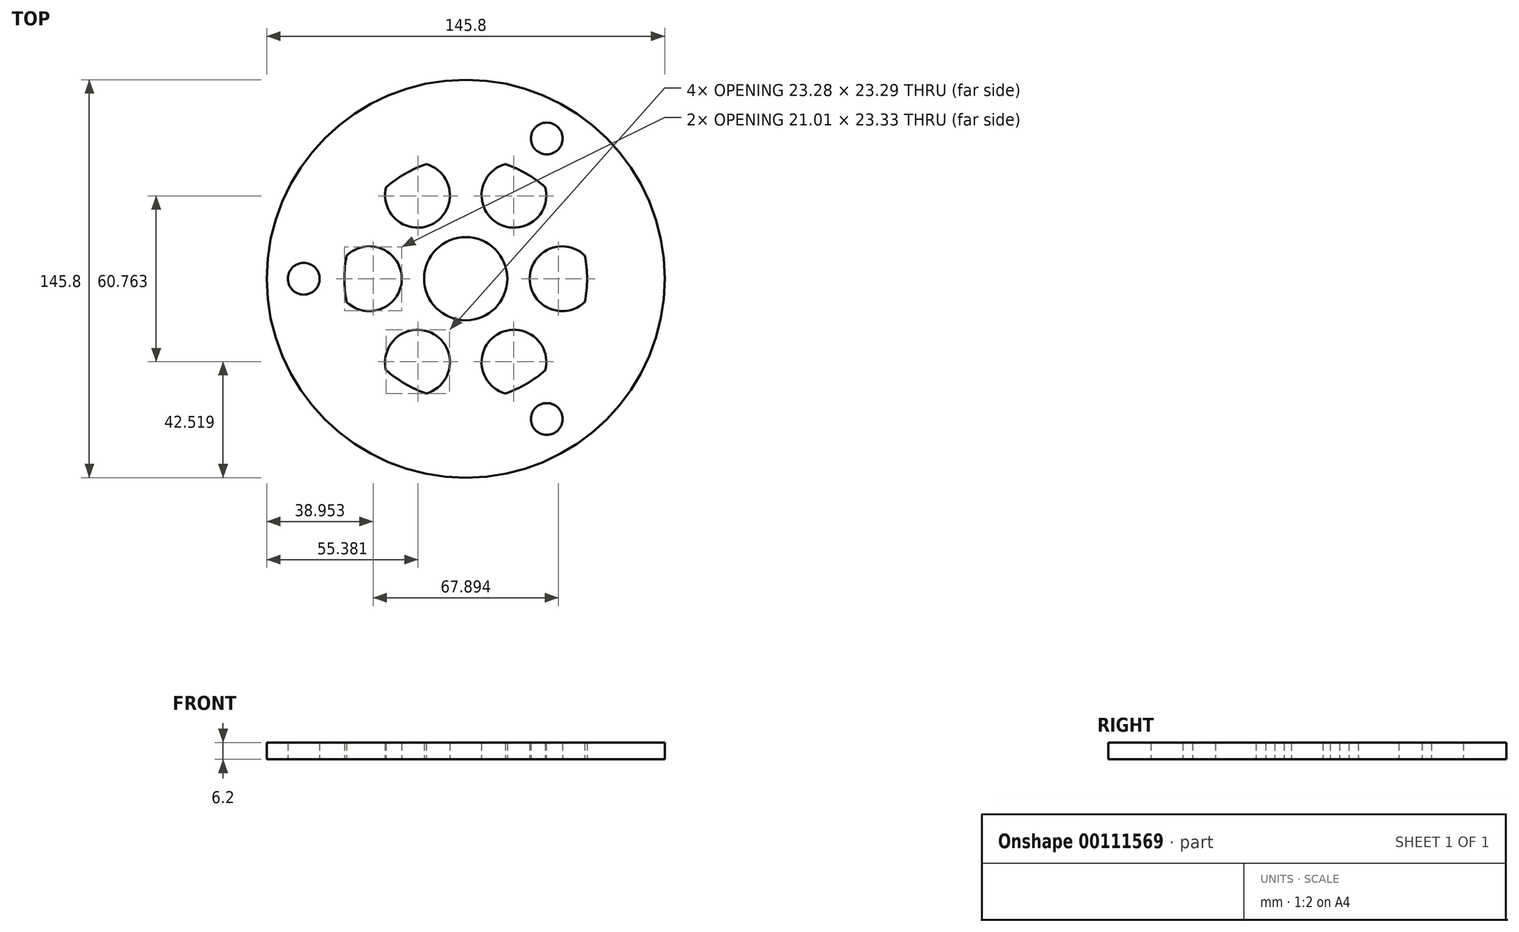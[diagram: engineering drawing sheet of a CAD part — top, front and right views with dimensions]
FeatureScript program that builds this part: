
annotation { "Feature Type Name" : "Feature", "Feature Type Description" : "" }
export const myFeature = defineFeature(function(context is Context, id is Id, definition is map)
    precondition{}
    {
        {
            var Q0;
            Q0=qCreatedBy(makeId("Top.planeOp"),FACE);
            var sketch = newSketch(context, id + "F0", { "sketchPlane" : qUnion([Q0])});
            skCircle(sketch, "E0", {"center": v(0, 0) * mm, "radius": 72.9 * mm});
            skCircle(sketch, "E1", {"center": v(0, 0) * mm, "radius": 15.24 * mm});
            skArc(sketch, "E2", {"start": v(-14.48, 42.03) * mm, "mid": v(-22.23, 38.5) * mm, "end": v(-29.16, 33.55) * mm});
            skArc(sketch, "E3", {"start": v(43.63, 8.48) * mm, "mid": v(23.44, 0) * mm, "end": v(43.63, -8.48) * mm});
            skArc(sketch, "E4.1.0", {"start": v(14.48, 42.03) * mm, "mid": v(11.72, 20.3) * mm, "end": v(29.16, 33.55) * mm});
            skArc(sketch, "E4.2.0", {"start": v(-29.16, 33.55) * mm, "mid": v(-11.72, 20.3) * mm, "end": v(-14.48, 42.03) * mm});
            skArc(sketch, "E4.3.0", {"start": v(-43.63, -8.48) * mm, "mid": v(-23.44, 0) * mm, "end": v(-43.63, 8.48) * mm});
            skArc(sketch, "E4.4.0", {"start": v(-14.48, -42.03) * mm, "mid": v(-11.72, -20.3) * mm, "end": v(-29.16, -33.55) * mm});
            skArc(sketch, "E4.5.0", {"start": v(29.16, -33.55) * mm, "mid": v(11.72, -20.3) * mm, "end": v(14.48, -42.03) * mm});
            skArc(sketch, "E5.trimOffspring", {"start": v(29.16, 33.55) * mm, "mid": v(22.23, 38.5) * mm, "end": v(14.48, 42.03) * mm});
            skArc(sketch, "E6.trimOffspring", {"start": v(43.63, -8.48) * mm, "mid": v(44.45, 0) * mm, "end": v(43.63, 8.48) * mm});
            skArc(sketch, "E7.trimOffspring", {"start": v(14.48, -42.03) * mm, "mid": v(22.22, -38.5) * mm, "end": v(29.16, -33.55) * mm});
            skArc(sketch, "E8.trimOffspring", {"start": v(-29.16, -33.55) * mm, "mid": v(-22.23, -38.5) * mm, "end": v(-14.48, -42.03) * mm});
            skArc(sketch, "E9.trimOffspring", {"start": v(-43.63, 8.48) * mm, "mid": v(-44.45, 0) * mm, "end": v(-43.63, -8.48) * mm});
            skCircle(sketch, "E10", {"center": v(-59.33, 0) * mm, "radius": 5.82 * mm});
            skPoint(sketch, "E10.centerSnap0", {"position": v(-44.45, 0) * mm});
            skCircle(sketch, "E11.1.0", {"center": v(29.67, -51.39) * mm, "radius": 5.82 * mm});
            skCircle(sketch, "E11.2.0", {"center": v(29.67, 51.39) * mm, "radius": 5.82 * mm});
            skSolve(sketch);
        }
        {
            var Q0;
            Q0 = qSketchRegion(id + "F0", true);
            extrude(context, id + "F1", {"entities" : qUnion([Q0]), "depth" : 6.2 * mm});
        }
    });
